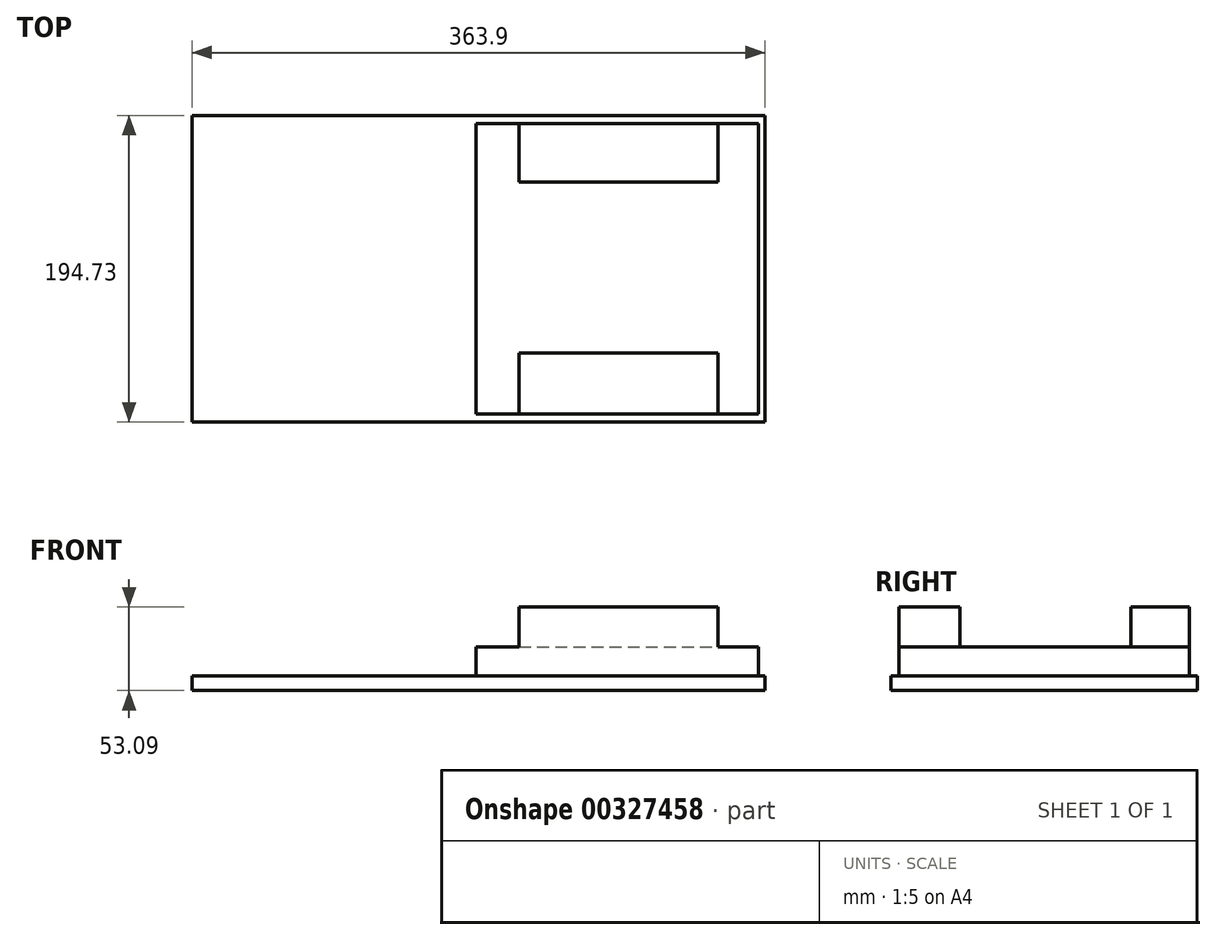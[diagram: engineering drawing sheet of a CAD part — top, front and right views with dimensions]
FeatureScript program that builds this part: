
annotation { "Feature Type Name" : "Feature", "Feature Type Description" : "" }
export const myFeature = defineFeature(function(context is Context, id is Id, definition is map)
    precondition{}
    {
        {
            var Q0;
            Q0=qCreatedBy(makeId("Top.planeOp"),FACE);
            var sketch = newSketch(context, id + "F0", { "sketchPlane" : qUnion([Q0])});
            skLineSegment(sketch, "E0.bottom", {"start": v(-180.34, -93.45) * mm, "end": v(183.56, -93.45) * mm});
            skLineSegment(sketch, "E0.top", {"start": v(-180.34, 101.28) * mm, "end": v(183.56, 101.28) * mm});
            skLineSegment(sketch, "E0.left", {"start": v(-180.34, -93.45) * mm, "end": v(-180.34, 101.28) * mm});
            skLineSegment(sketch, "E0.right", {"start": v(183.56, -93.45) * mm, "end": v(183.56, 101.28) * mm});
            skSolve(sketch);
        }
        {
            var Q0;
            Q0=makeQuery(id+"F0.imprint","IMPRINT",FACE,{"disambiguationData":[TD([[makeQuery(id+"F0.imprint","IMPRINT",EDGE,{"derivedFrom":sQuery(id+"F0.wireOp",EDGE,"E0.bottom")}),1.0]])]});
            var sketch = newSketch(context, id + "F1", { "sketchPlane" : qUnion([Q0])});
            skLineSegment(sketch, "E1.bottom", {"start": v(0, -88.47) * mm, "end": v(179.5, -88.47) * mm});
            skLineSegment(sketch, "E1.top", {"start": v(0, 96.14) * mm, "end": v(179.5, 96.14) * mm});
            skLineSegment(sketch, "E1.left", {"start": v(0, -88.47) * mm, "end": v(0, 96.14) * mm});
            skLineSegment(sketch, "E1.right", {"start": v(179.5, -88.47) * mm, "end": v(179.5, 96.14) * mm});
            skSolve(sketch);
        }
        {
            var Q0;
            Q0 = qSketchRegion(id + "F1", true);
            extrude(context, id + "F2", {"entities" : qUnion([Q0]), "depth" : 15 * mm});
        }
        {
            var Q0;
            Q0=makeQuery(id+"F2.opExtrude","CAP_FACE",FACE,{"disambiguationData":[OSD([sQuery(id+"F1.wireOp",EDGE,"E1.bottom"),sQuery(id+"F1.wireOp",EDGE,"E1.top"),sQuery(id+"F1.wireOp",EDGE,"E1.left"),sQuery(id+"F1.wireOp",EDGE,"E1.right")])],"isStart":false});
            extrude(context, id + "F3", {"entities" : qUnion([Q0]), "operationType" : NewBodyOperationType.ADD, "endBound" : BoundingType.SYMMETRIC, "depth" : 25.4 * mm});
        }
        {
            var Q0;
            Q0=makeQuery(id+"F3.opExtrude","CAP_FACE",FACE,{"disambiguationData":[OSD([sQuery(id+"F1.wireOp",EDGE,"E1.bottom"),sQuery(id+"F1.wireOp",EDGE,"E1.top"),sQuery(id+"F1.wireOp",EDGE,"E1.left"),sQuery(id+"F1.wireOp",EDGE,"E1.right")])],"isStart":false});
            var sketch = newSketch(context, id + "F4", { "sketchPlane" : qUnion([Q0])});
            skLineSegment(sketch, "E2.bottom", {"start": v(27.45, 96.14) * mm, "end": v(153.75, 96.14) * mm});
            skLineSegment(sketch, "E2.top", {"start": v(27.45, 58.88) * mm, "end": v(153.75, 58.88) * mm});
            skLineSegment(sketch, "E2.left", {"start": v(27.45, 96.14) * mm, "end": v(27.45, 58.88) * mm});
            skLineSegment(sketch, "E2.right", {"start": v(153.75, 96.14) * mm, "end": v(153.75, 58.88) * mm});
            skLineSegment(sketch, "E3.bottom", {"start": v(27.45, -88.47) * mm, "end": v(153.75, -88.47) * mm});
            skLineSegment(sketch, "E3.top", {"start": v(27.45, -49.57) * mm, "end": v(153.75, -49.57) * mm});
            skLineSegment(sketch, "E3.left", {"start": v(27.45, -88.47) * mm, "end": v(27.45, -49.57) * mm});
            skLineSegment(sketch, "E3.right", {"start": v(153.75, -88.47) * mm, "end": v(153.75, -49.57) * mm});
            skSolve(sketch);
        }
        {
            var Q0;
            Q0 = qSketchRegion(id + "F4", true);
            extrude(context, id + "F5", {"entities" : qUnion([Q0]), "operationType" : NewBodyOperationType.ADD, "depth" : 25.4 * mm});
        }
        {
            var Q0;
            Q0=makeQuery(id+"F0.imprint","IMPRINT",FACE,{"disambiguationData":[TD([[makeQuery(id+"F0.imprint","IMPRINT",EDGE,{"derivedFrom":sQuery(id+"F0.wireOp",EDGE,"E0.bottom")}),1.0]])]});
            extrude(context, id + "F6", {"entities" : qUnion([Q0]), "operationType" : NewBodyOperationType.ADD, "depth" : 9.4 * mm});
        }
    });
